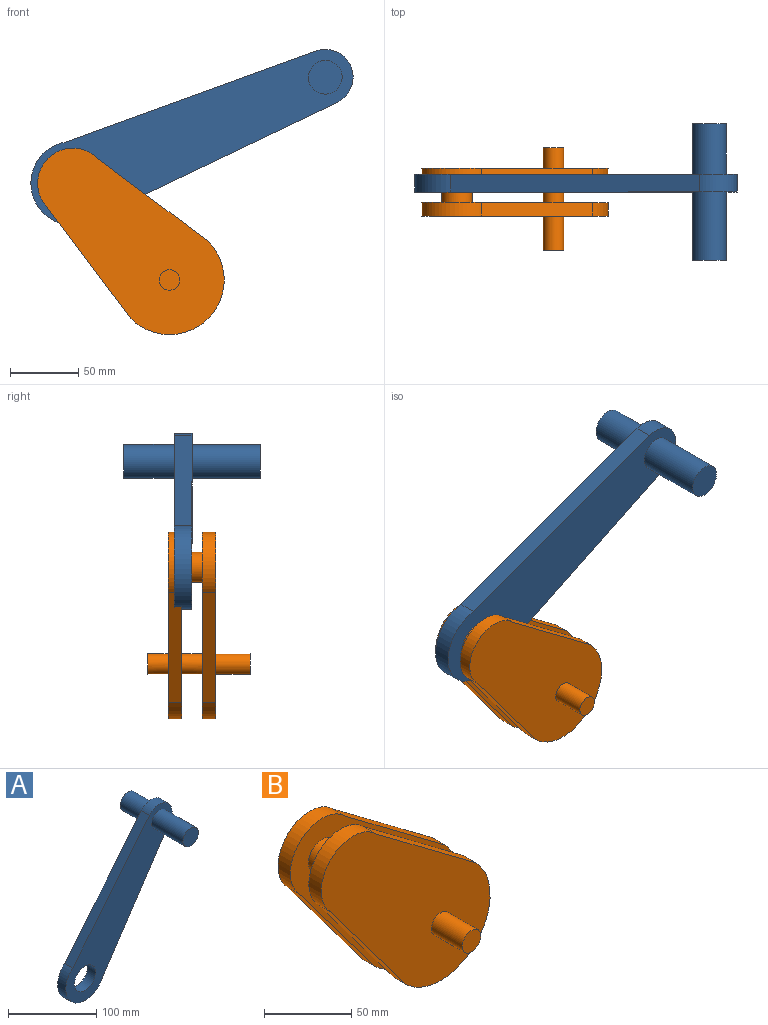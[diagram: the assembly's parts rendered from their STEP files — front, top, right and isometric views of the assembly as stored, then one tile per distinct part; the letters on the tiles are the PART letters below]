
ASSEMBLY  parts=2 mates=1
PART A: 11 faces, bbox 170x100x212.2 mm
  f0: cylinder r=30.7mm len=59.14mm, axis (0,1,0), area 1453.7mm2, adj f1,f3,f5,f6
  f1: plane 161.43x107.5mm, normal (0.83,0,-0.55), area 2521.4mm2, adj f0,f2,f5,f6
  f2: cylinder r=20.35mm len=36.11mm, axis (0,1,0), area 805.3mm2, adj f1,f3,f5,f6
  f3: plane 150.25x122.64mm, normal (-0.77,0,0.63), area 2521.4mm2, adj f0,f2,f5,f6
  f4: cylinder r=16.89mm len=33.78mm, axis (0,1,0), area 1379.8mm2, adj f5,f6
  f5: plane 212.22x170.05mm, normal (0,-1,0), area 10878.4mm2, adj f0,f1,f2,f3,f4,f9
  f6: plane 212.22x170.05mm, normal (0,1,0), area 10878.4mm2, adj f0,f1,f2,f3,f4,f8
  f7: plane 24.61x24.61mm, normal (0,1,0), area 475.9mm2, adj f8
  f8: cylinder r=12.31mm len=37mm, axis (0,1,0), area 2861.2mm2, adj f6,f7
  f9: cylinder r=12.31mm len=50mm, axis (0,1,0), area 3866.5mm2, adj f5,f10
  f10: plane 24.61x24.61mm, normal (0,-1,0), area 475.9mm2, adj f9
PART B: 18 faces, bbox 136.5x75x136.5 mm
  f0: cylinder r=7.5mm len=15mm, axis (0,1,0), area 706.9mm2, adj f6,f10
  f1: cylinder r=11.1mm len=22.19mm, axis (0,-1,0), area 1045.7mm2, adj f6,f10
  f2: plane 80.78x60.64mm, normal (0.6,0,0.8), area 1010.1mm2, adj f3,f5,f6,f7
  f3: cylinder r=25.76mm len=43.97mm, axis (0,-1,0), area 809.2mm2, adj f2,f4,f6,f7
  f4: plane 80.78x60.64mm, normal (-0.8,0,-0.6), area 1010.1mm2, adj f3,f5,f6,f7
  f5: cylinder r=40mm len=68.28mm, axis (0,-1,0), area 1256.6mm2, adj f2,f4,f6,f7
  f6: plane 136.47x136.47mm, normal (0,1,0), area 9567.8mm2, adj f0,f1,f2,f3,f4,f5
  f7: plane 136.47x136.47mm, normal (0,-1,0), area 9954.5mm2, adj f2,f3,f4,f5,f9
  f8: plane 15x15mm, normal (0,-1,0), area 176.7mm2, adj f9
  f9: cylinder r=7.5mm len=25mm, axis (0,1,0), area 1178.1mm2, adj f7,f8
  f10: plane 136.47x136.47mm, normal (0,-1,0), area 9567.8mm2, adj f0,f1,f11,f12,f13,f14
  f11: cylinder r=25.76mm len=43.97mm, axis (0,1,0), area 809.2mm2, adj f10,f12,f14,f17
  f12: plane 80.78x60.64mm, normal (0.6,0,0.8), area 1010.1mm2, adj f10,f11,f13,f17
  f13: cylinder r=40mm len=68.28mm, axis (0,1,0), area 1256.6mm2, adj f10,f12,f14,f17
  f14: plane 80.78x60.64mm, normal (-0.8,0,-0.6), area 1010.1mm2, adj f10,f11,f13,f17
  f15: plane 15x15mm, normal (0,1,0), area 176.7mm2, adj f16
  f16: cylinder r=7.5mm len=15mm, axis (0,1,0), area 706.9mm2, adj f15,f17
  f17: plane 136.47x136.47mm, normal (0,1,0), area 9954.5mm2, adj f11,f12,f13,f14,f16
PLACE A rot(axis=(0,1,0),30.8deg) t=(-217.17,12.61,143.4)mm
PLACE B t=(-171.04,7.11,169.62)mm fixed
MATE revolute A.f0 <-> B.f1  axis (0,-1,0) through (-241.75,24.61,240.33)mm
